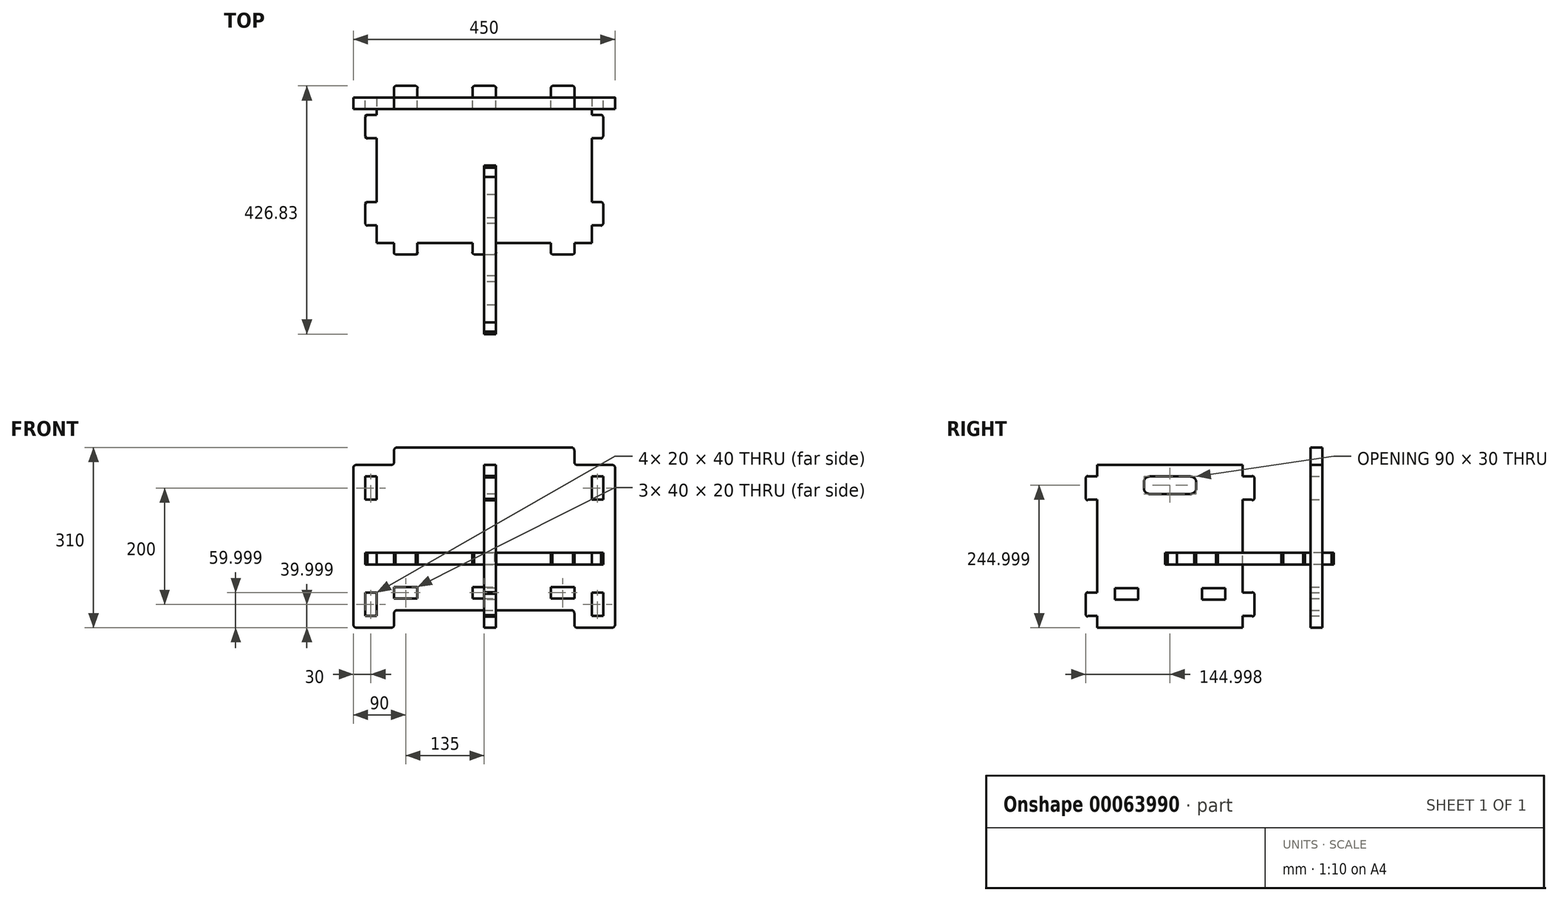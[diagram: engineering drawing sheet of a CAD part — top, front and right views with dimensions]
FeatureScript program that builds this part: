
annotation { "Feature Type Name" : "Feature", "Feature Type Description" : "" }
export const myFeature = defineFeature(function(context is Context, id is Id, definition is map)
    precondition{}
    {
        {
            var Q0;
            Q0=qCreatedBy(makeId("Front.planeOp"),FACE);
            var sketch = newSketch(context, id + "F0", { "sketchPlane" : qUnion([Q0])});
            skLineSegment(sketch, "E0.bottom", {"start": v(-150, -78.55) * mm, "end": v(150, -78.55) * mm});
            skLineSegment(sketch, "E0.top", {"start": v(-220, 171.45) * mm, "end": v(-160, 171.45) * mm});
            skLineSegment(sketch, "E0.left", {"start": v(-225, -78.55) * mm, "end": v(-225, 166.45) * mm});
            skLineSegment(sketch, "E0.right", {"start": v(225, -80.55) * mm, "end": v(225, 166.45) * mm});
            skLineSegment(sketch, "E1.bottom", {"start": v(-225, -78.55) * mm, "end": v(-155, -78.55) * mm});
            skLineSegment(sketch, "E1.top", {"start": v(-220, -108.55) * mm, "end": v(-160, -108.55) * mm});
            skLineSegment(sketch, "E1.left", {"start": v(-225, -78.55) * mm, "end": v(-225, -103.55) * mm});
            skLineSegment(sketch, "E1.right", {"start": v(-155, -83.55) * mm, "end": v(-155, -103.55) * mm});
            skLineSegment(sketch, "E2", {"start": v(0, -78.55) * mm, "end": v(0, 201.45) * mm, "construction": true});
            skLineSegment(sketch, "E3.MirrorCS", {"start": v(225, -78.55) * mm, "end": v(155, -78.55) * mm});
            skLineSegment(sketch, "E4.MirrorCS", {"start": v(220, -108.55) * mm, "end": v(160, -108.55) * mm});
            skLineSegment(sketch, "E5.MirrorCS", {"start": v(225, -78.55) * mm, "end": v(225, -103.55) * mm});
            skLineSegment(sketch, "E6.MirrorCS", {"start": v(155, -83.55) * mm, "end": v(155, -103.55) * mm});
            skLineSegment(sketch, "E7.bottom", {"start": v(-205, 171.45) * mm, "end": v(155, 171.45) * mm});
            skLineSegment(sketch, "E7.top", {"start": v(-150, 201.45) * mm, "end": v(150, 201.45) * mm});
            skLineSegment(sketch, "E7.left", {"start": v(-155, 176.45) * mm, "end": v(-155, 196.45) * mm});
            skLineSegment(sketch, "E7.right", {"start": v(155, 176.45) * mm, "end": v(155, 196.45) * mm});
            skLineSegment(sketch, "E8.bottom", {"start": v(-155, -58.55) * mm, "end": v(-115, -58.55) * mm});
            skLineSegment(sketch, "E8.top", {"start": v(-155, -38.55) * mm, "end": v(-115, -38.55) * mm});
            skLineSegment(sketch, "E8.left", {"start": v(-155, -58.55) * mm, "end": v(-155, -38.55) * mm});
            skLineSegment(sketch, "E8.right", {"start": v(-115, -58.55) * mm, "end": v(-115, -38.55) * mm});
            skLineSegment(sketch, "E9.bottom", {"start": v(-205, -88.55) * mm, "end": v(-185, -88.55) * mm});
            skLineSegment(sketch, "E9.top", {"start": v(-205, -48.55) * mm, "end": v(-185, -48.55) * mm});
            skLineSegment(sketch, "E9.left", {"start": v(-205, -88.55) * mm, "end": v(-205, -48.55) * mm});
            skLineSegment(sketch, "E9.right", {"start": v(-185, -88.55) * mm, "end": v(-185, -48.55) * mm});
            skLineSegment(sketch, "E10.MirrorCS", {"start": v(185, -88.55) * mm, "end": v(185, -48.55) * mm});
            skLineSegment(sketch, "E11.MirrorCS", {"start": v(205, -88.55) * mm, "end": v(185, -88.55) * mm});
            skLineSegment(sketch, "E12.MirrorCS", {"start": v(205, -88.55) * mm, "end": v(205, -48.55) * mm});
            skLineSegment(sketch, "E13.MirrorCS", {"start": v(205, -48.55) * mm, "end": v(185, -48.55) * mm});
            skLineSegment(sketch, "E14.MirrorCS", {"start": v(155, -58.55) * mm, "end": v(155, -38.55) * mm});
            skLineSegment(sketch, "E15.MirrorCS", {"start": v(155, -38.55) * mm, "end": v(115, -38.55) * mm});
            skLineSegment(sketch, "E16.MirrorCS", {"start": v(155, -58.55) * mm, "end": v(115, -58.55) * mm});
            skLineSegment(sketch, "E17.MirrorCS", {"start": v(115, -58.55) * mm, "end": v(115, -38.55) * mm});
            skLineSegment(sketch, "E18.bottom", {"start": v(-20, -58.55) * mm, "end": v(20, -58.55) * mm});
            skLineSegment(sketch, "E18.top", {"start": v(-20, -38.55) * mm, "end": v(20, -38.55) * mm});
            skLineSegment(sketch, "E18.left", {"start": v(-20, -58.55) * mm, "end": v(-20, -38.55) * mm});
            skLineSegment(sketch, "E18.right", {"start": v(20, -58.55) * mm, "end": v(20, -38.55) * mm});
            skLineSegment(sketch, "E19", {"start": v(0, -38.55) * mm, "end": v(0, -58.55) * mm, "construction": true});
            skPoint(sketch, "E20.visualSharp", {"position": v(-225, 171.45) * mm});
            skArc(sketch, "E20.filletArc", {"start": v(-220, 171.45) * mm, "mid": v(-223.54, 169.98) * mm, "end": v(-225, 166.45) * mm});
            skPoint(sketch, "E21.visualSharp", {"position": v(225, 171.45) * mm});
            skArc(sketch, "E21.filletArc", {"start": v(225, 166.45) * mm, "mid": v(223.54, 169.98) * mm, "end": v(220, 171.45) * mm});
            skPoint(sketch, "E22.visualSharp", {"position": v(225, -108.55) * mm});
            skArc(sketch, "E22.filletArc", {"start": v(220, -108.55) * mm, "mid": v(223.54, -107.09) * mm, "end": v(225, -103.55) * mm});
            skPoint(sketch, "E23.visualSharp", {"position": v(155, -108.55) * mm});
            skArc(sketch, "E23.filletArc", {"start": v(155, -103.55) * mm, "mid": v(156.46, -107.09) * mm, "end": v(160, -108.55) * mm});
            skPoint(sketch, "E24.visualSharp", {"position": v(-155, -108.55) * mm});
            skArc(sketch, "E24.filletArc", {"start": v(-160, -108.55) * mm, "mid": v(-156.46, -107.09) * mm, "end": v(-155, -103.55) * mm});
            skPoint(sketch, "E25.visualSharp", {"position": v(-225, -108.55) * mm});
            skArc(sketch, "E25.filletArc", {"start": v(-225, -103.55) * mm, "mid": v(-223.54, -107.09) * mm, "end": v(-220, -108.55) * mm});
            skArc(sketch, "E26.filletArc", {"start": v(-160, 171.45) * mm, "mid": v(-156.46, 172.91) * mm, "end": v(-155, 176.45) * mm});
            skPoint(sketch, "E27.visualSharp", {"position": v(-155, 201.45) * mm});
            skArc(sketch, "E27.filletArc", {"start": v(-150, 201.45) * mm, "mid": v(-153.54, 199.98) * mm, "end": v(-155, 196.45) * mm});
            skPoint(sketch, "E28.visualSharp", {"position": v(155, 201.45) * mm});
            skArc(sketch, "E28.filletArc", {"start": v(155, 196.45) * mm, "mid": v(153.54, 199.98) * mm, "end": v(150, 201.45) * mm});
            skLineSegment(sketch, "E29", {"start": v(160, 171.45) * mm, "end": v(220, 171.45) * mm});
            skPoint(sketch, "E30.visualSharp", {"position": v(155, 171.45) * mm});
            skArc(sketch, "E30.filletArc", {"start": v(155, 176.45) * mm, "mid": v(156.46, 172.91) * mm, "end": v(160, 171.45) * mm});
            skPoint(sketch, "E31.newPointA", {"position": v(-155, -80.55) * mm});
            skPoint(sketch, "E31.newPointB", {"position": v(-225, -78.55) * mm});
            skArc(sketch, "E31.filletArc", {"start": v(-150, -78.55) * mm, "mid": v(-153.54, -80.02) * mm, "end": v(-155, -83.55) * mm});
            skPoint(sketch, "E32.newPointA", {"position": v(155, -80.55) * mm});
            skPoint(sketch, "E32.newPointB", {"position": v(225, -78.55) * mm});
            skArc(sketch, "E32.filletArc", {"start": v(155, -83.55) * mm, "mid": v(153.54, -80.02) * mm, "end": v(150, -78.55) * mm});
            skLineSegment(sketch, "E33.MirrorCS", {"start": v(-205, 111.45) * mm, "end": v(-185, 111.45) * mm});
            skLineSegment(sketch, "E34.MirrorCS", {"start": v(-205, 151.45) * mm, "end": v(-205, 111.45) * mm});
            skLineSegment(sketch, "E35.MirrorCS", {"start": v(-205, 151.45) * mm, "end": v(-185, 151.45) * mm});
            skLineSegment(sketch, "E36.MirrorCS", {"start": v(-185, 151.45) * mm, "end": v(-185, 111.45) * mm});
            skLineSegment(sketch, "E37.MirrorCS", {"start": v(185, 151.45) * mm, "end": v(185, 111.45) * mm});
            skLineSegment(sketch, "E38.MirrorCS", {"start": v(205, 111.45) * mm, "end": v(185, 111.45) * mm});
            skLineSegment(sketch, "E39.MirrorCS", {"start": v(205, 151.45) * mm, "end": v(205, 111.45) * mm});
            skLineSegment(sketch, "E40.MirrorCS", {"start": v(205, 151.45) * mm, "end": v(185, 151.45) * mm});
            skLineSegment(sketch, "E41.bottom", {"start": v(185, -38.55) * mm, "end": v(-185, -38.55) * mm});
            skLineSegment(sketch, "E41.top", {"start": v(185, 171.45) * mm, "end": v(-185, 171.45) * mm});
            skLineSegment(sketch, "E41.left", {"start": v(185, -38.55) * mm, "end": v(185, 171.45) * mm});
            skLineSegment(sketch, "E41.right", {"start": v(-185, -38.55) * mm, "end": v(-185, 171.45) * mm});
            skSolve(sketch);
        }
        {
            var Q0;
            Q0=qCreatedBy(makeId("Right.planeOp"),FACE);
            var sketch = newSketch(context, id + "F1", { "sketchPlane" : qUnion([Q0])});
            skLineSegment(sketch, "E42.bottom", {"start": v(0, 196.45) * mm, "end": v(-136.83, 196.45) * mm, "construction": true});
            skLineSegment(sketch, "E42.top", {"start": v(0, -108.55) * mm, "end": v(-136.83, -108.55) * mm, "construction": true});
            skLineSegment(sketch, "E42.left", {"start": v(0, 196.45) * mm, "end": v(0, -108.55) * mm, "construction": true});
            skLineSegment(sketch, "E42.right", {"start": v(-136.83, 196.45) * mm, "end": v(-136.83, -108.55) * mm, "construction": true});
            skLineSegment(sketch, "E43.bottom", {"start": v(-136.83, -108.55) * mm, "end": v(-386.83, -108.55) * mm});
            skLineSegment(sketch, "E43.top", {"start": v(-136.83, 171.45) * mm, "end": v(-386.83, 171.45) * mm});
            skLineSegment(sketch, "E43.left", {"start": v(-136.83, -108.55) * mm, "end": v(-136.83, 171.45) * mm});
            skLineSegment(sketch, "E43.right", {"start": v(-386.83, -108.55) * mm, "end": v(-386.83, 171.45) * mm});
            skLineSegment(sketch, "E44.bottom", {"start": v(-136.83, 151.45) * mm, "end": v(-120.83, 151.45) * mm});
            skLineSegment(sketch, "E44.top", {"start": v(-136.83, 111.45) * mm, "end": v(-120.83, 111.45) * mm});
            skLineSegment(sketch, "E44.left", {"start": v(-136.83, 151.45) * mm, "end": v(-136.83, 111.45) * mm});
            skLineSegment(sketch, "E44.right", {"start": v(-120.83, 151.45) * mm, "end": v(-120.83, 111.45) * mm});
            skLineSegment(sketch, "E45.left", {"start": v(-120.83, 131.45) * mm, "end": v(-120.83, 111.45) * mm});
            skLineSegment(sketch, "E45.right", {"start": v(-116.83, 131.45) * mm, "end": v(-116.83, 112.95) * mm});
            skLineSegment(sketch, "E46", {"start": v(-136.83, 131.45) * mm, "end": v(-116.83, 131.45) * mm, "construction": true});
            skLineSegment(sketch, "E47", {"start": v(-120.83, 111.45) * mm, "end": v(-120.27, 110.9) * mm});
            skLineSegment(sketch, "E48", {"start": v(-118.85, 110.9) * mm, "end": v(-116.83, 112.95) * mm});
            skPoint(sketch, "E49.visualSharp", {"position": v(-119.56, 110.19) * mm});
            skArc(sketch, "E49.filletArc", {"start": v(-120.27, 110.9) * mm, "mid": v(-119.56, 110.6) * mm, "end": v(-118.85, 110.9) * mm});
            skLineSegment(sketch, "E50.MirrorCS", {"start": v(-118.85, 152) * mm, "end": v(-116.83, 149.95) * mm});
            skLineSegment(sketch, "E51.MirrorCS", {"start": v(-120.83, 151.45) * mm, "end": v(-120.27, 152) * mm});
            skArc(sketch, "E52.MirrorCS", {"start": v(-120.27, 152) * mm, "mid": v(-119.56, 152.3) * mm, "end": v(-118.85, 152) * mm});
            skPoint(sketch, "E53.MirrorP", {"position": v(-119.56, 152.7) * mm});
            skLineSegment(sketch, "E54.MirrorCS", {"start": v(-116.83, 131.45) * mm, "end": v(-116.83, 149.95) * mm});
            skLineSegment(sketch, "E55.MirrorCS", {"start": v(-120.83, 131.45) * mm, "end": v(-120.83, 151.45) * mm});
            skLineSegment(sketch, "E56", {"start": v(-386.83, 31.45) * mm, "end": v(-99.55, 31.45) * mm, "construction": true});
            skLineSegment(sketch, "E57.MirrorCS", {"start": v(-120.83, 111.45) * mm, "end": v(-120.83, 151.45) * mm});
            skLineSegment(sketch, "E58.MirrorCS", {"start": v(-136.83, 111.45) * mm, "end": v(-136.83, 151.45) * mm});
            skLineSegment(sketch, "E59.MirrorCS", {"start": v(-386.83, 231.45) * mm, "end": v(-99.55, 231.45) * mm, "construction": true});
            skArc(sketch, "E60.MirrorCS", {"start": v(-120.27, -48) * mm, "mid": v(-119.56, -47.7) * mm, "end": v(-118.85, -48) * mm});
            skLineSegment(sketch, "E61.MirrorCS", {"start": v(-120.83, -48.55) * mm, "end": v(-120.27, -48) * mm});
            skLineSegment(sketch, "E62.MirrorCS", {"start": v(-118.85, -48) * mm, "end": v(-116.83, -50.05) * mm});
            skLineSegment(sketch, "E63.MirrorCS", {"start": v(-118.85, -89.1) * mm, "end": v(-116.83, -87.05) * mm});
            skArc(sketch, "E64.MirrorCS", {"start": v(-120.27, -89.1) * mm, "mid": v(-119.56, -89.4) * mm, "end": v(-118.85, -89.1) * mm});
            skLineSegment(sketch, "E65.MirrorCS", {"start": v(-120.83, -88.55) * mm, "end": v(-120.27, -89.1) * mm});
            skLineSegment(sketch, "E66.MirrorCS", {"start": v(-120.83, -68.55) * mm, "end": v(-120.83, -88.55) * mm});
            skLineSegment(sketch, "E67.MirrorCS", {"start": v(-120.83, -48.55) * mm, "end": v(-120.83, -88.55) * mm});
            skLineSegment(sketch, "E68.MirrorCS", {"start": v(-120.83, -68.55) * mm, "end": v(-120.83, -48.55) * mm});
            skLineSegment(sketch, "E69.MirrorCS", {"start": v(-120.83, -88.55) * mm, "end": v(-120.83, -48.55) * mm});
            skLineSegment(sketch, "E70.MirrorCS", {"start": v(-116.83, -68.55) * mm, "end": v(-116.83, -50.05) * mm});
            skLineSegment(sketch, "E71.MirrorCS", {"start": v(-136.83, -88.55) * mm, "end": v(-120.83, -88.55) * mm});
            skLineSegment(sketch, "E72.MirrorCS", {"start": v(-136.83, -48.55) * mm, "end": v(-120.83, -48.55) * mm});
            skLineSegment(sketch, "E73.MirrorCS", {"start": v(-136.83, -88.55) * mm, "end": v(-136.83, -48.55) * mm});
            skPoint(sketch, "E74.MirrorP", {"position": v(-119.56, -47.3) * mm});
            skLineSegment(sketch, "E75.MirrorCS", {"start": v(-116.83, -68.55) * mm, "end": v(-116.83, -87.05) * mm});
            skLineSegment(sketch, "E76.MirrorCS", {"start": v(-136.83, -48.55) * mm, "end": v(-136.83, -88.55) * mm});
            skPoint(sketch, "E77.MirrorP", {"position": v(-119.56, -89.81) * mm});
            skLineSegment(sketch, "E78.MirrorCS", {"start": v(-136.83, -68.55) * mm, "end": v(-116.83, -68.55) * mm, "construction": true});
            skLineSegment(sketch, "E79", {"start": v(-261.83, 171.45) * mm, "end": v(-261.83, -148.14) * mm, "construction": true});
            skLineSegment(sketch, "E80.MirrorCS", {"start": v(-402.83, -88.55) * mm, "end": v(-403.4, -89.1) * mm});
            skLineSegment(sketch, "E81.MirrorCS", {"start": v(-402.83, -48.55) * mm, "end": v(-403.4, -48) * mm});
            skArc(sketch, "E82.MirrorCS", {"start": v(-403.4, -89.1) * mm, "mid": v(-404.1, -89.4) * mm, "end": v(-404.81, -89.1) * mm});
            skLineSegment(sketch, "E83.MirrorCS", {"start": v(-404.81, -89.1) * mm, "end": v(-406.83, -87.05) * mm});
            skArc(sketch, "E84.MirrorCS", {"start": v(-403.4, -48) * mm, "mid": v(-404.1, -47.7) * mm, "end": v(-404.81, -48) * mm});
            skLineSegment(sketch, "E85.MirrorCS", {"start": v(-404.81, -48) * mm, "end": v(-406.83, -50.05) * mm});
            skLineSegment(sketch, "E86.MirrorCS", {"start": v(-402.83, -48.55) * mm, "end": v(-402.83, -88.55) * mm});
            skLineSegment(sketch, "E87.MirrorCS", {"start": v(-402.83, -68.55) * mm, "end": v(-402.83, -48.55) * mm});
            skLineSegment(sketch, "E88.MirrorCS", {"start": v(-402.83, -68.55) * mm, "end": v(-402.83, -88.55) * mm});
            skLineSegment(sketch, "E89.MirrorCS", {"start": v(-402.83, -88.55) * mm, "end": v(-402.83, -48.55) * mm});
            skPoint(sketch, "E90.MirrorP", {"position": v(-404.1, -47.3) * mm});
            skLineSegment(sketch, "E91.MirrorCS", {"start": v(-386.83, -48.55) * mm, "end": v(-402.83, -48.55) * mm});
            skLineSegment(sketch, "E92.MirrorCS", {"start": v(-406.83, -68.55) * mm, "end": v(-406.83, -87.05) * mm});
            skLineSegment(sketch, "E93.MirrorCS", {"start": v(-386.83, -48.55) * mm, "end": v(-386.83, -88.55) * mm});
            skLineSegment(sketch, "E94.MirrorCS", {"start": v(-386.83, -88.55) * mm, "end": v(-402.83, -88.55) * mm});
            skLineSegment(sketch, "E95.MirrorCS", {"start": v(-406.83, -68.55) * mm, "end": v(-406.83, -50.05) * mm});
            skLineSegment(sketch, "E96.MirrorCS", {"start": v(-386.83, -88.55) * mm, "end": v(-386.83, -48.55) * mm});
            skPoint(sketch, "E97.MirrorP", {"position": v(-404.1, -89.81) * mm});
            skLineSegment(sketch, "E98.MirrorCS", {"start": v(-386.83, -68.55) * mm, "end": v(-406.83, -68.55) * mm, "construction": true});
            skLineSegment(sketch, "E99.MirrorCS", {"start": v(-402.83, 111.45) * mm, "end": v(-403.4, 110.9) * mm});
            skLineSegment(sketch, "E100.MirrorCS", {"start": v(-402.83, 151.45) * mm, "end": v(-403.4, 152) * mm});
            skLineSegment(sketch, "E101.MirrorCS", {"start": v(-404.81, 110.9) * mm, "end": v(-406.83, 112.95) * mm});
            skArc(sketch, "E102.MirrorCS", {"start": v(-403.4, 110.9) * mm, "mid": v(-404.1, 110.6) * mm, "end": v(-404.81, 110.9) * mm});
            skLineSegment(sketch, "E103.MirrorCS", {"start": v(-404.81, 152) * mm, "end": v(-406.83, 149.95) * mm});
            skArc(sketch, "E104.MirrorCS", {"start": v(-403.4, 152) * mm, "mid": v(-404.1, 152.3) * mm, "end": v(-404.81, 152) * mm});
            skLineSegment(sketch, "E105.MirrorCS", {"start": v(-402.83, 111.45) * mm, "end": v(-402.83, 151.45) * mm});
            skLineSegment(sketch, "E106.MirrorCS", {"start": v(-402.83, 131.45) * mm, "end": v(-402.83, 111.45) * mm});
            skLineSegment(sketch, "E107.MirrorCS", {"start": v(-402.83, 131.45) * mm, "end": v(-402.83, 151.45) * mm});
            skLineSegment(sketch, "E108.MirrorCS", {"start": v(-402.83, 151.45) * mm, "end": v(-402.83, 111.45) * mm});
            skPoint(sketch, "E109.MirrorP", {"position": v(-404.1, 110.19) * mm});
            skLineSegment(sketch, "E110.MirrorCS", {"start": v(-386.83, 111.45) * mm, "end": v(-402.83, 111.45) * mm});
            skLineSegment(sketch, "E111.MirrorCS", {"start": v(-386.83, 151.45) * mm, "end": v(-386.83, 111.45) * mm});
            skLineSegment(sketch, "E112.MirrorCS", {"start": v(-406.83, 131.45) * mm, "end": v(-406.83, 112.95) * mm});
            skLineSegment(sketch, "E113.MirrorCS", {"start": v(-386.83, 151.45) * mm, "end": v(-402.83, 151.45) * mm});
            skLineSegment(sketch, "E114.MirrorCS", {"start": v(-406.83, 131.45) * mm, "end": v(-406.83, 149.95) * mm});
            skLineSegment(sketch, "E115.MirrorCS", {"start": v(-386.83, 111.45) * mm, "end": v(-386.83, 151.45) * mm});
            skPoint(sketch, "E116.MirrorP", {"position": v(-404.1, 152.7) * mm});
            skLineSegment(sketch, "E117.MirrorCS", {"start": v(-386.83, 131.45) * mm, "end": v(-406.83, 131.45) * mm, "construction": true});
            skLineSegment(sketch, "E118.bottom", {"start": v(-226.83, 151.45) * mm, "end": v(-296.83, 151.45) * mm});
            skLineSegment(sketch, "E118.top", {"start": v(-226.83, 121.45) * mm, "end": v(-296.83, 121.45) * mm});
            skLineSegment(sketch, "E118.left", {"start": v(-216.83, 141.45) * mm, "end": v(-216.83, 131.45) * mm});
            skLineSegment(sketch, "E118.right", {"start": v(-306.83, 141.45) * mm, "end": v(-306.83, 131.45) * mm});
            skLineSegment(sketch, "E119", {"start": v(-261.83, 151.45) * mm, "end": v(-261.83, 121.45) * mm, "construction": true});
            skPoint(sketch, "E120.visualSharp", {"position": v(-216.83, 151.45) * mm});
            skArc(sketch, "E120.filletArc", {"start": v(-216.83, 141.45) * mm, "mid": v(-219.76, 148.52) * mm, "end": v(-226.83, 151.45) * mm});
            skPoint(sketch, "E121.visualSharp", {"position": v(-216.83, 121.45) * mm});
            skArc(sketch, "E121.filletArc", {"start": v(-226.83, 121.45) * mm, "mid": v(-219.76, 124.38) * mm, "end": v(-216.83, 131.45) * mm});
            skPoint(sketch, "E122.visualSharp", {"position": v(-306.83, 151.45) * mm});
            skArc(sketch, "E122.filletArc", {"start": v(-296.83, 151.45) * mm, "mid": v(-303.9, 148.52) * mm, "end": v(-306.83, 141.45) * mm});
            skPoint(sketch, "E123.visualSharp", {"position": v(-306.83, 121.45) * mm});
            skArc(sketch, "E123.filletArc", {"start": v(-306.83, 131.45) * mm, "mid": v(-303.9, 124.38) * mm, "end": v(-296.83, 121.45) * mm});
            skLineSegment(sketch, "E124.bottom", {"start": v(-356.83, -40.55) * mm, "end": v(-316.83, -40.55) * mm});
            skLineSegment(sketch, "E124.top", {"start": v(-356.83, -60.55) * mm, "end": v(-316.83, -60.55) * mm});
            skLineSegment(sketch, "E124.left", {"start": v(-356.83, -40.55) * mm, "end": v(-356.83, -60.55) * mm});
            skLineSegment(sketch, "E124.right", {"start": v(-316.83, -40.55) * mm, "end": v(-316.83, -60.55) * mm});
            skLineSegment(sketch, "E125.MirrorCS", {"start": v(-166.83, -40.55) * mm, "end": v(-206.83, -40.55) * mm});
            skLineSegment(sketch, "E126.MirrorCS", {"start": v(-166.83, -60.55) * mm, "end": v(-206.83, -60.55) * mm});
            skLineSegment(sketch, "E127.MirrorCS", {"start": v(-166.83, -40.55) * mm, "end": v(-166.83, -60.55) * mm});
            skLineSegment(sketch, "E128.MirrorCS", {"start": v(-206.83, -40.55) * mm, "end": v(-206.83, -60.55) * mm});
            skSolve(sketch);
        }
        {
            var Q0;
            Q0=qCreatedBy(makeId("Top.planeOp"),FACE);
            var sketch = newSketch(context, id + "F2", { "sketchPlane" : qUnion([Q0])});
            skLineSegment(sketch, "E129.bottom", {"start": v(-250, 0) * mm, "end": v(250, 0) * mm, "construction": true});
            skLineSegment(sketch, "E130.bottom", {"start": v(-185, 0) * mm, "end": v(185, 0) * mm});
            skLineSegment(sketch, "E130.top", {"start": v(-185, -250) * mm, "end": v(185, -250) * mm});
            skLineSegment(sketch, "E130.left", {"start": v(-185, 0) * mm, "end": v(-185, -250) * mm});
            skLineSegment(sketch, "E130.right", {"start": v(185, 0) * mm, "end": v(185, -250) * mm});
            skLineSegment(sketch, "E131.bottom", {"start": v(-155, 0) * mm, "end": v(-115, 0) * mm});
            skLineSegment(sketch, "E131.top", {"start": v(-155, 16) * mm, "end": v(-115, 16) * mm});
            skLineSegment(sketch, "E131.left", {"start": v(-155, 0) * mm, "end": v(-155, 16) * mm});
            skLineSegment(sketch, "E131.right", {"start": v(-115, 0) * mm, "end": v(-115, 16) * mm});
            skLineSegment(sketch, "E132.bottom", {"start": v(-155, 16) * mm, "end": v(-135, 16) * mm});
            skLineSegment(sketch, "E132.top", {"start": v(-152.5, 20) * mm, "end": v(-135, 20) * mm});
            skLineSegment(sketch, "E133", {"start": v(-135, 0) * mm, "end": v(-135, 20) * mm, "construction": true});
            skLineSegment(sketch, "E134", {"start": v(-155, 16) * mm, "end": v(-155.26, 16.3) * mm});
            skLineSegment(sketch, "E135", {"start": v(-155.15, 17.7) * mm, "end": v(-152.5, 20) * mm});
            skPoint(sketch, "E136.visualSharp", {"position": v(-155.91, 17.05) * mm});
            skArc(sketch, "E136.filletArc", {"start": v(-155.15, 17.7) * mm, "mid": v(-155.5, 17.02) * mm, "end": v(-155.26, 16.3) * mm});
            skLineSegment(sketch, "E137.MirrorCS", {"start": v(-114.85, 17.7) * mm, "end": v(-117.5, 20) * mm});
            skLineSegment(sketch, "E138.MirrorCS", {"start": v(-115, 16) * mm, "end": v(-114.74, 16.3) * mm});
            skArc(sketch, "E139.MirrorCS", {"start": v(-114.85, 17.7) * mm, "mid": v(-114.5, 17.02) * mm, "end": v(-114.74, 16.3) * mm});
            skLineSegment(sketch, "E140.MirrorCS", {"start": v(-117.5, 20) * mm, "end": v(-135, 20) * mm});
            skLineSegment(sketch, "E141.MirrorCS", {"start": v(-115, 16) * mm, "end": v(-135, 16) * mm});
            skPoint(sketch, "E142.MirrorP", {"position": v(-114.09, 17.05) * mm});
            skLineSegment(sketch, "E143.MirrorCS", {"start": v(155.15, 17.7) * mm, "end": v(152.5, 20) * mm});
            skLineSegment(sketch, "E144.MirrorCS", {"start": v(155, 16) * mm, "end": v(155.26, 16.3) * mm});
            skLineSegment(sketch, "E145.MirrorCS", {"start": v(114.85, 17.7) * mm, "end": v(117.5, 20) * mm});
            skArc(sketch, "E146.MirrorCS", {"start": v(114.85, 17.7) * mm, "mid": v(114.5, 17.02) * mm, "end": v(114.74, 16.3) * mm});
            skArc(sketch, "E147.MirrorCS", {"start": v(155.15, 17.7) * mm, "mid": v(155.5, 17.02) * mm, "end": v(155.26, 16.3) * mm});
            skLineSegment(sketch, "E148.MirrorCS", {"start": v(115, 16) * mm, "end": v(114.74, 16.3) * mm});
            skPoint(sketch, "E149.MirrorP", {"position": v(155.91, 17.05) * mm});
            skLineSegment(sketch, "E150.MirrorCS", {"start": v(155, 16) * mm, "end": v(115, 16) * mm});
            skLineSegment(sketch, "E151.MirrorCS", {"start": v(135, 0) * mm, "end": v(135, 20) * mm, "construction": true});
            skLineSegment(sketch, "E152.MirrorCS", {"start": v(152.5, 20) * mm, "end": v(135, 20) * mm});
            skLineSegment(sketch, "E153.MirrorCS", {"start": v(117.5, 20) * mm, "end": v(135, 20) * mm});
            skLineSegment(sketch, "E154.MirrorCS", {"start": v(155, 16) * mm, "end": v(135, 16) * mm});
            skLineSegment(sketch, "E155.MirrorCS", {"start": v(115, 0) * mm, "end": v(115, 16) * mm});
            skLineSegment(sketch, "E156.MirrorCS", {"start": v(155, 0) * mm, "end": v(155, 16) * mm});
            skLineSegment(sketch, "E157.MirrorCS", {"start": v(155, 0) * mm, "end": v(115, 0) * mm});
            skLineSegment(sketch, "E158.MirrorCS", {"start": v(115, 16) * mm, "end": v(135, 16) * mm});
            skPoint(sketch, "E159.MirrorP", {"position": v(114.09, 17.05) * mm});
            skLineSegment(sketch, "E160", {"start": v(185, -125) * mm, "end": v(-327.24, -125) * mm, "construction": true});
            skPoint(sketch, "E160.endSnap0", {"position": v(-185, -125) * mm});
            skLineSegment(sketch, "E161.MirrorCS", {"start": v(-115, -266) * mm, "end": v(-114.74, -266.3) * mm});
            skLineSegment(sketch, "E162.MirrorCS", {"start": v(-114.85, -267.7) * mm, "end": v(-117.5, -270) * mm});
            skArc(sketch, "E163.MirrorCS", {"start": v(-114.85, -267.7) * mm, "mid": v(-114.5, -267.02) * mm, "end": v(-114.74, -266.3) * mm});
            skLineSegment(sketch, "E164.MirrorCS", {"start": v(-155, -266) * mm, "end": v(-115, -266) * mm});
            skLineSegment(sketch, "E165.MirrorCS", {"start": v(-117.5, -270) * mm, "end": v(-135, -270) * mm});
            skLineSegment(sketch, "E166.MirrorCS", {"start": v(-155, -266) * mm, "end": v(-135, -266) * mm});
            skLineSegment(sketch, "E167.MirrorCS", {"start": v(-115, -266) * mm, "end": v(-135, -266) * mm});
            skLineSegment(sketch, "E168.MirrorCS", {"start": v(-155, -250) * mm, "end": v(-155, -266) * mm});
            skLineSegment(sketch, "E169.MirrorCS", {"start": v(-115, -250) * mm, "end": v(-115, -266) * mm});
            skLineSegment(sketch, "E170.MirrorCS", {"start": v(-155, -250) * mm, "end": v(-115, -250) * mm});
            skLineSegment(sketch, "E171.MirrorCS", {"start": v(-135, -250) * mm, "end": v(-135, -270) * mm, "construction": true});
            skPoint(sketch, "E172.MirrorP", {"position": v(-114.09, -267.05) * mm});
            skLineSegment(sketch, "E173.bottom", {"start": v(-185, -30) * mm, "end": v(-201, -30) * mm});
            skLineSegment(sketch, "E173.top", {"start": v(-185, -70) * mm, "end": v(-201, -70) * mm});
            skLineSegment(sketch, "E173.left", {"start": v(-185, -30) * mm, "end": v(-185, -70) * mm});
            skLineSegment(sketch, "E174", {"start": v(-67.5, 0) * mm, "end": v(-67.5, 57.2) * mm, "construction": true});
            skLineSegment(sketch, "E175.MirrorCS", {"start": v(-115, 16) * mm, "end": v(-155, 16) * mm});
            skLineSegment(sketch, "E176.MirrorCS", {"start": v(-115, 0) * mm, "end": v(-155, 0) * mm});
            skLineSegment(sketch, "E177.MirrorCS", {"start": v(20, 16) * mm, "end": v(20.26, 16.3) * mm});
            skArc(sketch, "E178.MirrorCS", {"start": v(20.15, 17.7) * mm, "mid": v(20.5, 17.02) * mm, "end": v(20.26, 16.3) * mm});
            skLineSegment(sketch, "E179.MirrorCS", {"start": v(-20, 16) * mm, "end": v(-20.26, 16.3) * mm});
            skLineSegment(sketch, "E180.MirrorCS", {"start": v(-20.15, 17.7) * mm, "end": v(-17.5, 20) * mm});
            skArc(sketch, "E181.MirrorCS", {"start": v(-20.15, 17.7) * mm, "mid": v(-20.5, 17.02) * mm, "end": v(-20.26, 16.3) * mm});
            skLineSegment(sketch, "E182.MirrorCS", {"start": v(20.15, 17.7) * mm, "end": v(17.5, 20) * mm});
            skLineSegment(sketch, "E183.MirrorCS", {"start": v(-20, 16) * mm, "end": v(0, 16) * mm});
            skLineSegment(sketch, "E184.MirrorCS", {"start": v(20, 16) * mm, "end": v(0, 16) * mm});
            skLineSegment(sketch, "E185.MirrorCS", {"start": v(-20, 0) * mm, "end": v(-20, 16) * mm});
            skLineSegment(sketch, "E186.MirrorCS", {"start": v(20, 0) * mm, "end": v(20, 16) * mm});
            skPoint(sketch, "E187.MirrorP", {"position": v(-20.91, 17.05) * mm});
            skLineSegment(sketch, "E188.MirrorCS", {"start": v(-17.5, 20) * mm, "end": v(0, 20) * mm});
            skLineSegment(sketch, "E189.MirrorCS", {"start": v(20, 0) * mm, "end": v(-20, 0) * mm});
            skLineSegment(sketch, "E190.MirrorCS", {"start": v(17.5, 20) * mm, "end": v(0, 20) * mm});
            skPoint(sketch, "E191.MirrorP", {"position": v(20.91, 17.05) * mm});
            skLineSegment(sketch, "E192.MirrorCS", {"start": v(20, 16) * mm, "end": v(-20, 16) * mm});
            skLineSegment(sketch, "E193.MirrorCS", {"start": v(-20, 0) * mm, "end": v(20, 0) * mm});
            skLineSegment(sketch, "E194.MirrorCS", {"start": v(0, 0) * mm, "end": v(0, 20) * mm, "construction": true});
            skLineSegment(sketch, "E195.MirrorCS", {"start": v(-20, 16) * mm, "end": v(20, 16) * mm});
            skLineSegment(sketch, "E196.MirrorCS", {"start": v(-20, -266) * mm, "end": v(-20.26, -266.3) * mm});
            skLineSegment(sketch, "E197.MirrorCS", {"start": v(20, -266) * mm, "end": v(20.26, -266.3) * mm});
            skArc(sketch, "E198.MirrorCS", {"start": v(-20.15, -267.7) * mm, "mid": v(-20.5, -267.02) * mm, "end": v(-20.26, -266.3) * mm});
            skArc(sketch, "E199.MirrorCS", {"start": v(20.15, -267.7) * mm, "mid": v(20.5, -267.02) * mm, "end": v(20.26, -266.3) * mm});
            skLineSegment(sketch, "E200.MirrorCS", {"start": v(-20.15, -267.7) * mm, "end": v(-17.5, -270) * mm});
            skLineSegment(sketch, "E201.MirrorCS", {"start": v(20.15, -267.7) * mm, "end": v(17.5, -270) * mm});
            skLineSegment(sketch, "E202.MirrorCS", {"start": v(-20, -266) * mm, "end": v(0, -266) * mm});
            skLineSegment(sketch, "E203.MirrorCS", {"start": v(20, -266) * mm, "end": v(0, -266) * mm});
            skLineSegment(sketch, "E204.MirrorCS", {"start": v(17.5, -270) * mm, "end": v(0, -270) * mm});
            skPoint(sketch, "E205.MirrorP", {"position": v(-20.91, -267.05) * mm});
            skLineSegment(sketch, "E206.MirrorCS", {"start": v(-20, -250) * mm, "end": v(20, -250) * mm});
            skPoint(sketch, "E207.MirrorP", {"position": v(20.91, -267.05) * mm});
            skLineSegment(sketch, "E208.MirrorCS", {"start": v(-20, -250) * mm, "end": v(-20, -266) * mm});
            skLineSegment(sketch, "E209.MirrorCS", {"start": v(20, -250) * mm, "end": v(20, -266) * mm});
            skLineSegment(sketch, "E210.MirrorCS", {"start": v(20, -266) * mm, "end": v(-20, -266) * mm});
            skLineSegment(sketch, "E211.MirrorCS", {"start": v(-17.5, -270) * mm, "end": v(0, -270) * mm});
            skLineSegment(sketch, "E212.MirrorCS", {"start": v(-20, -266) * mm, "end": v(20, -266) * mm});
            skLineSegment(sketch, "E213.MirrorCS", {"start": v(20, -250) * mm, "end": v(-20, -250) * mm});
            skLineSegment(sketch, "E214.MirrorCS", {"start": v(0, -250) * mm, "end": v(0, -270) * mm, "construction": true});
            skLineSegment(sketch, "E215", {"start": v(-185, -50) * mm, "end": v(-205, -50) * mm, "construction": true});
            skPoint(sketch, "E216.MirrorP", {"position": v(185, -125) * mm});
            skLineSegment(sketch, "E217", {"start": v(0, 149.48) * mm, "end": v(0, -285.17) * mm, "construction": true});
            skLineSegment(sketch, "E218.MirrorCS", {"start": v(115, -266) * mm, "end": v(114.74, -266.3) * mm});
            skArc(sketch, "E219.MirrorCS", {"start": v(114.85, -267.7) * mm, "mid": v(114.5, -267.02) * mm, "end": v(114.74, -266.3) * mm});
            skLineSegment(sketch, "E220.MirrorCS", {"start": v(114.85, -267.7) * mm, "end": v(117.5, -270) * mm});
            skLineSegment(sketch, "E221.MirrorCS", {"start": v(155, -266) * mm, "end": v(115, -266) * mm});
            skLineSegment(sketch, "E222.MirrorCS", {"start": v(117.5, -270) * mm, "end": v(135, -270) * mm});
            skPoint(sketch, "E223.MirrorP", {"position": v(114.09, -267.05) * mm});
            skLineSegment(sketch, "E224.MirrorCS", {"start": v(115, -250) * mm, "end": v(115, -266) * mm});
            skLineSegment(sketch, "E225.MirrorCS", {"start": v(155, -250) * mm, "end": v(115, -250) * mm});
            skLineSegment(sketch, "E226.MirrorCS", {"start": v(155, -250) * mm, "end": v(155, -266) * mm});
            skLineSegment(sketch, "E227.MirrorCS", {"start": v(135, -250) * mm, "end": v(135, -270) * mm, "construction": true});
            skLineSegment(sketch, "E228.MirrorCS", {"start": v(115, -266) * mm, "end": v(135, -266) * mm});
            skLineSegment(sketch, "E229.MirrorCS", {"start": v(155, -266) * mm, "end": v(135, -266) * mm});
            skLineSegment(sketch, "E230", {"start": v(-201, -70) * mm, "end": v(-201, -30) * mm});
            skLineSegment(sketch, "E231.right", {"start": v(-230, -50) * mm, "end": v(-230, -70) * mm, "construction": true});
            skArc(sketch, "E232.filletArc", {"start": v(-201.26, -29.84) * mm, "mid": v(-201.92, -29.7) * mm, "end": v(-202.52, -30) * mm});
            skLineSegment(sketch, "E233", {"start": v(-201.26, -29.84) * mm, "end": v(-201, -30) * mm});
            skLineSegment(sketch, "E234", {"start": v(-205, -50) * mm, "end": v(-205, -33) * mm});
            skLineSegment(sketch, "E235", {"start": v(-202.52, -30) * mm, "end": v(-205, -33) * mm});
            skLineSegment(sketch, "E236.MirrorCS", {"start": v(-201.26, -70.16) * mm, "end": v(-201, -70) * mm});
            skArc(sketch, "E237.MirrorCS", {"start": v(-201.26, -70.16) * mm, "mid": v(-201.92, -70.3) * mm, "end": v(-202.52, -70) * mm});
            skLineSegment(sketch, "E238.MirrorCS", {"start": v(-202.52, -70) * mm, "end": v(-205, -67) * mm});
            skLineSegment(sketch, "E239.MirrorCS", {"start": v(-205, -50) * mm, "end": v(-205, -67) * mm});
            skLineSegment(sketch, "E240.MirrorCS", {"start": v(-201.26, -220.16) * mm, "end": v(-201, -220) * mm});
            skLineSegment(sketch, "E241.MirrorCS", {"start": v(-201.26, -179.84) * mm, "end": v(-201, -180) * mm});
            skArc(sketch, "E242.MirrorCS", {"start": v(-201.26, -220.16) * mm, "mid": v(-201.92, -220.3) * mm, "end": v(-202.52, -220) * mm});
            skArc(sketch, "E243.MirrorCS", {"start": v(-201.26, -179.84) * mm, "mid": v(-201.92, -179.7) * mm, "end": v(-202.52, -180) * mm});
            skLineSegment(sketch, "E244.MirrorCS", {"start": v(-202.52, -220) * mm, "end": v(-205, -217) * mm});
            skLineSegment(sketch, "E245.MirrorCS", {"start": v(-202.52, -180) * mm, "end": v(-205, -183) * mm});
            skLineSegment(sketch, "E246.MirrorCS", {"start": v(-201, -180) * mm, "end": v(-201, -220) * mm});
            skLineSegment(sketch, "E247.MirrorCS", {"start": v(-185, -200) * mm, "end": v(-205, -200) * mm, "construction": true});
            skLineSegment(sketch, "E248.MirrorCS", {"start": v(-205, -200) * mm, "end": v(-205, -183) * mm});
            skLineSegment(sketch, "E249.MirrorCS", {"start": v(-185, -220) * mm, "end": v(-201, -220) * mm});
            skLineSegment(sketch, "E250.MirrorCS", {"start": v(-205, -200) * mm, "end": v(-205, -217) * mm});
            skLineSegment(sketch, "E251.MirrorCS", {"start": v(-185, -180) * mm, "end": v(-201, -180) * mm});
            skLineSegment(sketch, "E252.MirrorCS", {"start": v(-185, -220) * mm, "end": v(-185, -180) * mm});
            skLineSegment(sketch, "E253.MirrorCS", {"start": v(-155, -266) * mm, "end": v(-155.26, -266.3) * mm});
            skArc(sketch, "E254.MirrorCS", {"start": v(-155.15, -267.7) * mm, "mid": v(-155.5, -267.02) * mm, "end": v(-155.26, -266.3) * mm});
            skLineSegment(sketch, "E255.MirrorCS", {"start": v(-155.15, -267.7) * mm, "end": v(-152.5, -270) * mm});
            skLineSegment(sketch, "E256.MirrorCS", {"start": v(-152.5, -270) * mm, "end": v(-135, -270) * mm});
            skPoint(sketch, "E257.MirrorP", {"position": v(-155.91, -267.05) * mm});
            skLineSegment(sketch, "E258.MirrorCS", {"start": v(155, -266) * mm, "end": v(155.26, -266.3) * mm});
            skArc(sketch, "E259.MirrorCS", {"start": v(155.15, -267.7) * mm, "mid": v(155.5, -267.02) * mm, "end": v(155.26, -266.3) * mm});
            skLineSegment(sketch, "E260.MirrorCS", {"start": v(155.15, -267.7) * mm, "end": v(152.5, -270) * mm});
            skLineSegment(sketch, "E261.MirrorCS", {"start": v(152.5, -270) * mm, "end": v(135, -270) * mm});
            skPoint(sketch, "E262.MirrorP", {"position": v(155.91, -267.05) * mm});
            skLineSegment(sketch, "E263.MirrorCS", {"start": v(201.26, -29.84) * mm, "end": v(201, -30) * mm});
            skArc(sketch, "E264.MirrorCS", {"start": v(201.26, -29.84) * mm, "mid": v(201.92, -29.7) * mm, "end": v(202.52, -30) * mm});
            skLineSegment(sketch, "E265.MirrorCS", {"start": v(202.52, -70) * mm, "end": v(205, -67) * mm});
            skLineSegment(sketch, "E266.MirrorCS", {"start": v(201.26, -70.16) * mm, "end": v(201, -70) * mm});
            skArc(sketch, "E267.MirrorCS", {"start": v(201.26, -70.16) * mm, "mid": v(201.92, -70.3) * mm, "end": v(202.52, -70) * mm});
            skLineSegment(sketch, "E268.MirrorCS", {"start": v(202.52, -30) * mm, "end": v(205, -33) * mm});
            skLineSegment(sketch, "E269.MirrorCS", {"start": v(201, -70) * mm, "end": v(201, -30) * mm});
            skLineSegment(sketch, "E270.MirrorCS", {"start": v(205, -50) * mm, "end": v(205, -67) * mm});
            skLineSegment(sketch, "E271.MirrorCS", {"start": v(185, -30) * mm, "end": v(185, -70) * mm});
            skLineSegment(sketch, "E272.MirrorCS", {"start": v(185, -30) * mm, "end": v(201, -30) * mm});
            skLineSegment(sketch, "E273.MirrorCS", {"start": v(205, -50) * mm, "end": v(205, -33) * mm});
            skLineSegment(sketch, "E274.MirrorCS", {"start": v(185, -50) * mm, "end": v(205, -50) * mm, "construction": true});
            skLineSegment(sketch, "E275.MirrorCS", {"start": v(185, -70) * mm, "end": v(201, -70) * mm});
            skArc(sketch, "E276.MirrorCS", {"start": v(201.26, -220.16) * mm, "mid": v(201.92, -220.3) * mm, "end": v(202.52, -220) * mm});
            skLineSegment(sketch, "E277.MirrorCS", {"start": v(201.26, -179.84) * mm, "end": v(201, -180) * mm});
            skLineSegment(sketch, "E278.MirrorCS", {"start": v(201.26, -220.16) * mm, "end": v(201, -220) * mm});
            skArc(sketch, "E279.MirrorCS", {"start": v(201.26, -179.84) * mm, "mid": v(201.92, -179.7) * mm, "end": v(202.52, -180) * mm});
            skLineSegment(sketch, "E280.MirrorCS", {"start": v(202.52, -180) * mm, "end": v(205, -183) * mm});
            skLineSegment(sketch, "E281.MirrorCS", {"start": v(202.52, -220) * mm, "end": v(205, -217) * mm});
            skLineSegment(sketch, "E282.MirrorCS", {"start": v(201, -180) * mm, "end": v(201, -220) * mm});
            skLineSegment(sketch, "E283.MirrorCS", {"start": v(185, -180) * mm, "end": v(201, -180) * mm});
            skLineSegment(sketch, "E284.MirrorCS", {"start": v(205, -200) * mm, "end": v(205, -217) * mm});
            skLineSegment(sketch, "E285.MirrorCS", {"start": v(185, -220) * mm, "end": v(201, -220) * mm});
            skLineSegment(sketch, "E286.MirrorCS", {"start": v(185, -200) * mm, "end": v(205, -200) * mm, "construction": true});
            skLineSegment(sketch, "E287.MirrorCS", {"start": v(185, -220) * mm, "end": v(185, -180) * mm});
            skLineSegment(sketch, "E288.MirrorCS", {"start": v(205, -200) * mm, "end": v(205, -183) * mm});
            skSolve(sketch);
        }
        {
            var Q0;
            Q0=qSketchRegion(id+"F0",true);
            extrude(context, id + "F3", {"entities" : qUnion([Q0]), "depth" : 20 * mm});
        }
        {
            var Q0;
            Q0=qSketchRegion(id+"F1",true);
            extrude(context, id + "F4", {"entities" : qUnion([Q0]), "depth" : 20 * mm});
        }
        {
            var Q0;
            Q0=qSketchRegion(id+"F2",true);
            extrude(context, id + "F5", {"entities" : qUnion([Q0]), "depth" : 20 * mm});
        }
    });
